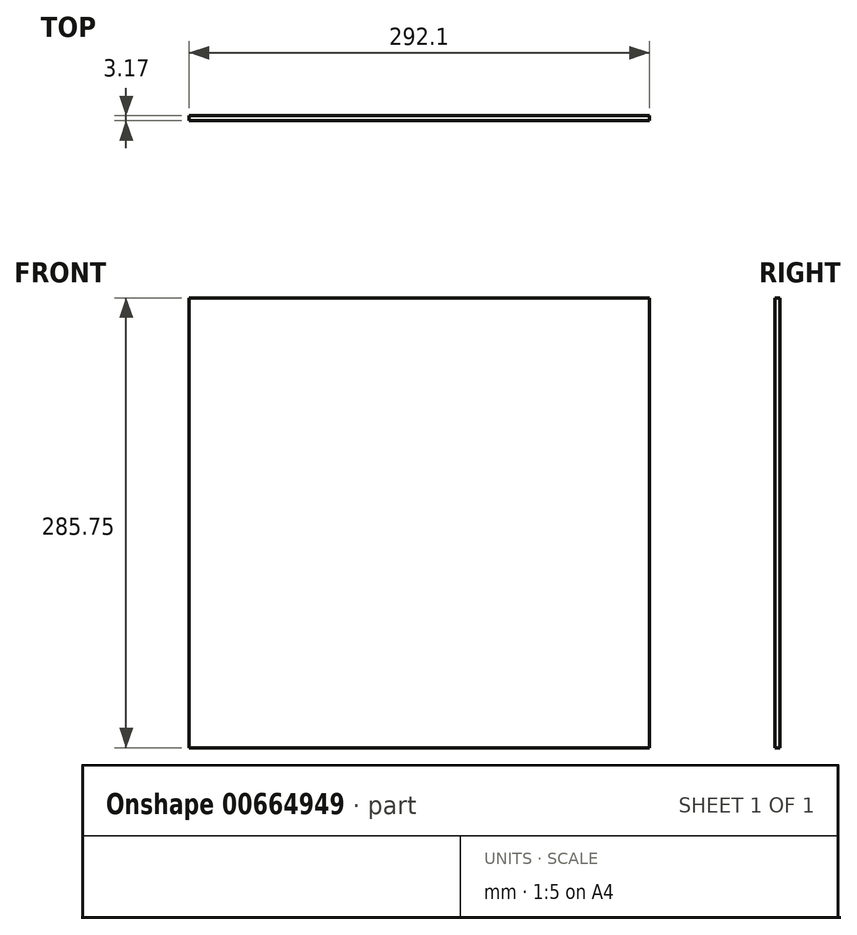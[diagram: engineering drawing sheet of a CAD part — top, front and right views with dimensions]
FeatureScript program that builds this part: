
annotation { "Feature Type Name" : "Feature", "Feature Type Description" : "" }
export const myFeature = defineFeature(function(context is Context, id is Id, definition is map)
    precondition{}
    {
        {
            var Q0;
            Q0=qCreatedBy(makeId("Front.planeOp"),FACE);
            var sketch = newSketch(context, id + "F0", { "sketchPlane" : qUnion([Q0])});
            skLineSegment(sketch, "E0.bottom", {"start": v(0, 0) * mm, "end": v(292.1, 0) * mm});
            skLineSegment(sketch, "E0.top", {"start": v(0, 285.75) * mm, "end": v(292.1, 285.75) * mm});
            skLineSegment(sketch, "E0.left", {"start": v(0, 0) * mm, "end": v(0, 285.75) * mm});
            skLineSegment(sketch, "E0.right", {"start": v(292.1, 0) * mm, "end": v(292.1, 285.75) * mm});
            skSolve(sketch);
        }
        {
            var Q0;
            Q0=makeQuery(id+"F0.imprint","IMPRINT",FACE,{"disambiguationData":[TD([[makeQuery(id+"F0.imprint","IMPRINT",EDGE,{"derivedFrom":sQuery(id+"F0.wireOp",EDGE,"E0.bottom")}),1.0]])]});
            extrude(context, id + "F1", {"entities" : qUnion([Q0]), "depth" : 3.17 * mm, "offsetDistance" : 25.4 * mm});
        }
    });
